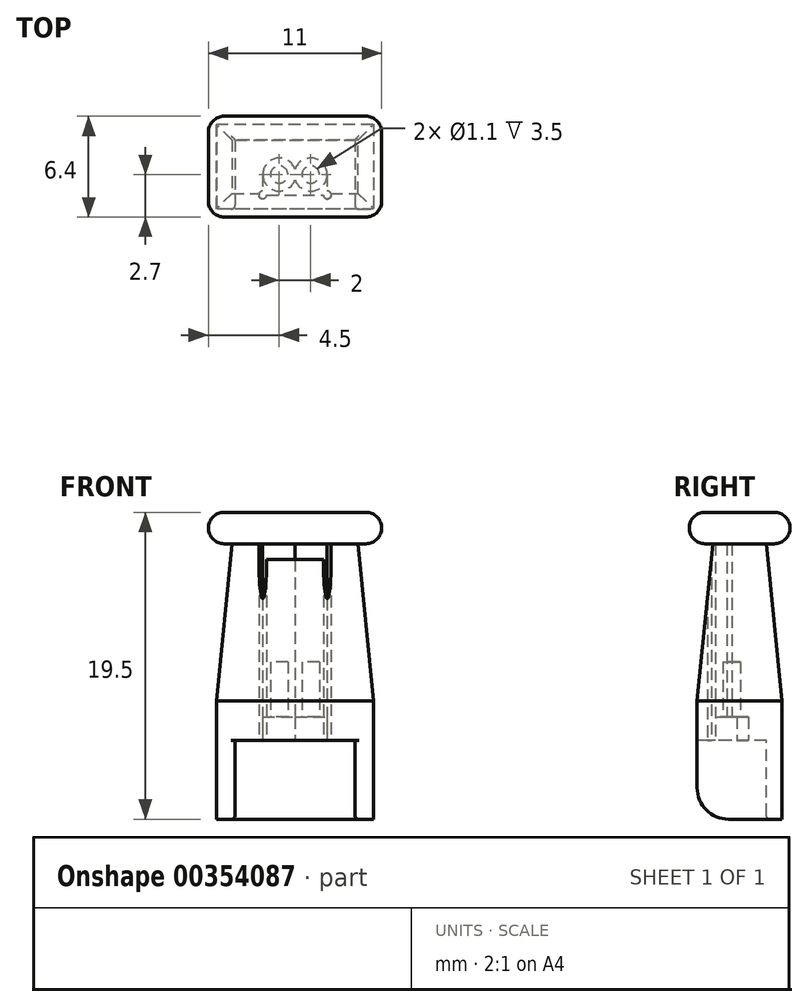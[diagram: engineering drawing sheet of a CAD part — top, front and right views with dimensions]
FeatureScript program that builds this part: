
annotation { "Feature Type Name" : "Feature", "Feature Type Description" : "" }
export const myFeature = defineFeature(function(context is Context, id is Id, definition is map)
    precondition{}
    {
        {
            var Q0;
            Q0=qCreatedBy(makeId("Top.planeOp"),FACE);
            var sketch = newSketch(context, id + "F0", { "sketchPlane" : qUnion([Q0])});
            skCircle(sketch, "E0", {"center": v(1, 0) * mm, "radius": 1.05 * mm});
            skCircle(sketch, "E1.MirrorC", {"center": v(-1, 0) * mm, "radius": 1.05 * mm});
            skLineSegment(sketch, "E2.top", {"start": v(-3.8, -2.2) * mm, "end": v(3.8, -2.2) * mm});
            skCircle(sketch, "E3", {"center": v(-2.05, 1.3) * mm, "radius": 0.25 * mm, "construction": true});
            skCircle(sketch, "E4.MirrorC", {"center": v(2.05, 1.3) * mm, "radius": 0.25 * mm, "construction": true});
            skCircle(sketch, "E5.MirrorC", {"center": v(-2.05, -1.3) * mm, "radius": 0.25 * mm, "construction": true});
            skCircle(sketch, "E6.MirrorC", {"center": v(2.05, -1.3) * mm, "radius": 0.25 * mm, "construction": true});
            skLineSegment(sketch, "E7", {"start": v(-1, 0) * mm, "end": v(1, 0) * mm, "construction": true});
            skPoint(sketch, "E8", {"position": v(0, 0) * mm});
            skLineSegment(sketch, "E9.bottom", {"start": v(2.05, 1.3) * mm, "end": v(-2.05, 1.3) * mm, "construction": true});
            skLineSegment(sketch, "E9.top", {"start": v(2.05, -1.3) * mm, "end": v(-2.05, -1.3) * mm, "construction": true});
            skLineSegment(sketch, "E9.left", {"start": v(2.05, 1.3) * mm, "end": v(2.05, -1.3) * mm, "construction": true});
            skLineSegment(sketch, "E9.right", {"start": v(-2.05, 1.3) * mm, "end": v(-2.05, -1.3) * mm, "construction": true});
            skArc(sketch, "E10", {"start": v(-1.8, 1.3) * mm, "mid": v(-2.23, 1.48) * mm, "end": v(-2.05, 1.05) * mm});
            skArc(sketch, "E11.MirrorCS", {"start": v(1.8, 1.3) * mm, "mid": v(2.23, 1.48) * mm, "end": v(2.05, 1.05) * mm});
            skArc(sketch, "E12.MirrorCS", {"start": v(-1.8, -1.3) * mm, "mid": v(-2.23, -1.48) * mm, "end": v(-2.05, -1.05) * mm});
            skArc(sketch, "E13.MirrorCS", {"start": v(1.8, -1.3) * mm, "mid": v(2.23, -1.48) * mm, "end": v(2.05, -1.05) * mm});
            skLineSegment(sketch, "E14", {"start": v(-2.05, 1.05) * mm, "end": v(-2.05, -1.05) * mm});
            skLineSegment(sketch, "E15", {"start": v(2.05, 1.05) * mm, "end": v(2.05, -1.05) * mm});
            skLineSegment(sketch, "E16", {"start": v(-1.8, 1.3) * mm, "end": v(1.8, 1.3) * mm});
            skLineSegment(sketch, "E17", {"start": v(-1.8, -1.3) * mm, "end": v(1.8, -1.3) * mm});
            skCircle(sketch, "E18", {"center": v(-1, 0) * mm, "radius": 0.55 * mm});
            skCircle(sketch, "E19", {"center": v(1, 0) * mm, "radius": 0.55 * mm});
            skPoint(sketch, "E20", {"position": v(0, -2.2) * mm});
            skLineSegment(sketch, "E21", {"start": v(0, 0) * mm, "end": v(0, -2.2) * mm, "construction": true});
            skLineSegment(sketch, "E22.MirrorCS", {"start": v(-3.8, 2.2) * mm, "end": v(3.8, 2.2) * mm});
            skLineSegment(sketch, "E23", {"start": v(3.8, 2.2) * mm, "end": v(3.8, -2.2) * mm});
            skLineSegment(sketch, "E24.bottom", {"start": v(-3.8, 2.2) * mm, "end": v(-5, 2.2) * mm});
            skLineSegment(sketch, "E24.top", {"start": v(-3.8, -2.2) * mm, "end": v(-5, -2.2) * mm});
            skLineSegment(sketch, "E24.left", {"start": v(-3.8, 2.2) * mm, "end": v(-3.8, -2.2) * mm});
            skLineSegment(sketch, "E24.right", {"start": v(-5, 2.2) * mm, "end": v(-5, -2.2) * mm});
            skLineSegment(sketch, "E25.MirrorCS", {"start": v(3.8, 2.2) * mm, "end": v(5, 2.2) * mm});
            skLineSegment(sketch, "E26.MirrorCS", {"start": v(5, 2.2) * mm, "end": v(5, -2.2) * mm});
            skLineSegment(sketch, "E27.MirrorCS", {"start": v(3.8, -2.2) * mm, "end": v(5, -2.2) * mm});
            skLineSegment(sketch, "E28", {"start": v(-5, 2.2) * mm, "end": v(-5, 3.2) * mm});
            skLineSegment(sketch, "E29.MirrorCS", {"start": v(5, 2.2) * mm, "end": v(5, 3.2) * mm});
            skLineSegment(sketch, "E30", {"start": v(-5, 3.2) * mm, "end": v(5, 3.2) * mm});
            skSolve(sketch);
        }
        {
            var Q0;
            Q0=makeQuery(id+"F0.imprint","IMPRINT",FACE,{"disambiguationData":[TD([[makeQuery(id+"F0.imprint","IMPRINT",EDGE,{"derivedFrom":sQuery(id+"F0.wireOp",EDGE,"E22.MirrorCS")}),1.0]])]});
            var Q1;
            Q1=makeQuery(id+"F0.imprint","IMPRINT",FACE,{"disambiguationData":[TD([[makeQuery(id+"F0.imprint","IMPRINT",EDGE,{"derivedFrom":sQuery(id+"F0.wireOp",EDGE,"E24.bottom")}),1.0]])]});
            var Q2;
            Q2=makeQuery(id+"F0.imprint","IMPRINT",FACE,{"disambiguationData":[TD([[makeQuery(id+"F0.imprint","IMPRINT",EDGE,{"derivedFrom":sQuery(id+"F0.wireOp",EDGE,"E2.top")}),1.0]])]});
            var Q3;
            Q3=makeQuery(id+"F0.imprint","IMPRINT",FACE,{"disambiguationData":[TD([[makeQuery(id+"F0.imprint","IMPRINT",EDGE,{"derivedFrom":sQuery(id+"F0.wireOp",EDGE,"E23")}),1.0]])]});
            var Q4;
            {var subQ0=sQuery(id+"F0.wireOp",EDGE,"E10");Q4=makeQuery(id+"F0.imprint","IMPRINT",FACE,{"disambiguationData":[TD([[makeQuery(id+"F0.imprint","IMPRINT",EDGE,{"derivedFrom":subQ0}),1.0]])]});}
            var Q5;
            {var subQ0=sQuery(id+"F0.wireOp",EDGE,"E12.MirrorCS");Q5=makeQuery(id+"F0.imprint","IMPRINT",FACE,{"disambiguationData":[TD([[makeQuery(id+"F0.imprint","IMPRINT",EDGE,{"derivedFrom":subQ0}),-1.0]])]});}
            var Q6;
            Q6=makeQuery(id+"F0.imprint","IMPRINT",FACE,{"disambiguationData":[TD([[makeQuery(id+"F0.imprint","IMPRINT",EDGE,{"derivedFrom":sQuery(id+"F0.wireOp",EDGE,"E18")}),-1.0]])]});
            var Q7;
            Q7=makeQuery(id+"F0.imprint","IMPRINT",FACE,{"disambiguationData":[TD([[makeQuery(id+"F0.imprint","IMPRINT",EDGE,{"derivedFrom":sQuery(id+"F0.wireOp",EDGE,"E19")}),-1.0]])]});
            var Q8;
            Q8=makeQuery(id+"F0.imprint","IMPRINT",FACE,{"disambiguationData":[TD([[makeQuery(id+"F0.imprint","IMPRINT",EDGE,{"derivedFrom":sQuery(id+"F0.wireOp",EDGE,"E18")}),1.0]])]});
            var Q9;
            Q9=makeQuery(id+"F0.imprint","IMPRINT",FACE,{"disambiguationData":[TD([[makeQuery(id+"F0.imprint","IMPRINT",EDGE,{"derivedFrom":sQuery(id+"F0.wireOp",EDGE,"E19")}),1.0]])]});
            var Q10;
            {var subQ0=sQuery(id+"F0.wireOp",EDGE,"E1.MirrorC");var subQ1=sQuery(id+"F0.wireOp",EDGE,"E0");var subQ2=makeQuery(id+"F0.imprint","INTERSECT",VERTEX,{"disambiguationData":[OD(0.0)],"derivedFrom":[subQ1,subQ0]});Q10=makeQuery(id+"F0.imprint","IMPRINT",FACE,{"disambiguationData":[TD([[makeQuery(id+"F0.imprint","IMPRINT",EDGE,{"disambiguationData":[TD([[subQ2,-1.0]])],"derivedFrom":subQ1}),1.0]])]});}
            extrude(context, id + "F1", {"entities" : qUnion([Q0, Q1, Q2, Q3, Q4, Q5, Q6, Q7, Q8, Q9, Q10]), "depth" : 12.5 * mm, "offsetDistance" : 25 * mm});
        }
        {
            var Q0;
            Q0=makeQuery(id+"F0.imprint","IMPRINT",FACE,{"disambiguationData":[TD([[makeQuery(id+"F0.imprint","IMPRINT",EDGE,{"derivedFrom":sQuery(id+"F0.wireOp",EDGE,"E24.bottom")}),1.0]])]});
            var Q1;
            Q1=makeQuery(id+"F0.imprint","IMPRINT",FACE,{"disambiguationData":[TD([[makeQuery(id+"F0.imprint","IMPRINT",EDGE,{"derivedFrom":sQuery(id+"F0.wireOp",EDGE,"E23")}),1.0]])]});
            var Q2;
            Q2=makeQuery(id+"F0.imprint","IMPRINT",FACE,{"disambiguationData":[TD([[makeQuery(id+"F0.imprint","IMPRINT",EDGE,{"derivedFrom":sQuery(id+"F0.wireOp",EDGE,"E22.MirrorCS")}),1.0]])]});
            extrude(context, id + "F2", {"entities" : qUnion([Q0, Q1, Q2]), "operationType" : NewBodyOperationType.ADD, "oppositeDirection" : true, "depth" : 5 * mm, "offsetDistance" : 25 * mm});
        }
        {
            var Q0;
            Q0=makeQuery(id+"F0.imprint","IMPRINT",FACE,{"disambiguationData":[TD([[makeQuery(id+"F0.imprint","IMPRINT",EDGE,{"derivedFrom":sQuery(id+"F0.wireOp",EDGE,"E18")}),-1.0]])]});
            var Q1;
            Q1=makeQuery(id+"F0.imprint","IMPRINT",FACE,{"disambiguationData":[TD([[makeQuery(id+"F0.imprint","IMPRINT",EDGE,{"derivedFrom":sQuery(id+"F0.wireOp",EDGE,"E19")}),-1.0]])]});
            var Q2;
            {var subQ0=sQuery(id+"F0.wireOp",EDGE,"E1.MirrorC");var subQ1=sQuery(id+"F0.wireOp",EDGE,"E0");var subQ2=makeQuery(id+"F0.imprint","INTERSECT",VERTEX,{"disambiguationData":[OD(0.0)],"derivedFrom":[subQ1,subQ0]});Q2=makeQuery(id+"F0.imprint","IMPRINT",FACE,{"disambiguationData":[TD([[makeQuery(id+"F0.imprint","IMPRINT",EDGE,{"disambiguationData":[TD([[subQ2,-1.0]])],"derivedFrom":subQ1}),1.0]])]});}
            extrude(context, id + "F3", {"entities" : qUnion([Q0, Q1, Q2]), "operationType" : NewBodyOperationType.REMOVE, "depth" : 1.5 * mm, "offsetDistance" : 25 * mm});
        }
        {
            var Q0;
            Q0=makeQuery(id+"F0.imprint","IMPRINT",FACE,{"disambiguationData":[TD([[makeQuery(id+"F0.imprint","IMPRINT",EDGE,{"derivedFrom":sQuery(id+"F0.wireOp",EDGE,"E18")}),1.0]])]});
            var Q1;
            Q1=makeQuery(id+"F0.imprint","IMPRINT",FACE,{"disambiguationData":[TD([[makeQuery(id+"F0.imprint","IMPRINT",EDGE,{"derivedFrom":sQuery(id+"F0.wireOp",EDGE,"E19")}),1.0]])]});
            extrude(context, id + "F4", {"entities" : qUnion([Q0, Q1]), "operationType" : NewBodyOperationType.REMOVE, "depth" : 5 * mm, "offsetDistance" : 25 * mm});
        }
        {
            var Q0;
            Q0=makeQuery(id+"F2.opExtrude","CAP_EDGE",EDGE,{"disambiguationData":[OSD([sQuery(id+"F0.wireOp",EDGE,"E27.MirrorCS")])],"isStart":false});
            var Q1;
            Q1=makeQuery(id+"F2.opExtrude","CAP_EDGE",EDGE,{"disambiguationData":[OSD([sQuery(id+"F0.wireOp",EDGE,"E24.top")])],"isStart":false});
            fillet(context, id + "F5", {"entities" : qUnion([Q0, Q1]), "radius" : 2 * mm, "tangentPropagation" : true, "allowEdgeOverflow" : false});
        }
        {
            var Q0;
            Q0=makeQuery(id+"F3.boolean.opBoolean","COPY",EDGE,{"derivedFrom":makeQuery(id+"F3.opExtrude","CAP_EDGE",EDGE,{"disambiguationData":[OSD([sQuery(id+"F0.wireOp",EDGE,"E19")])],"isStart":false})});
            var Q1;
            Q1=makeQuery(id+"F3.boolean.opBoolean","COPY",EDGE,{"derivedFrom":makeQuery(id+"F3.opExtrude","CAP_EDGE",EDGE,{"disambiguationData":[OSD([sQuery(id+"F0.wireOp",EDGE,"E0")])],"isStart":true})});
            var Q2;
            Q2=makeQuery(id+"F3.boolean.opBoolean","COPY",EDGE,{"derivedFrom":makeQuery(id+"F3.opExtrude","CAP_EDGE",EDGE,{"disambiguationData":[OSD([sQuery(id+"F0.wireOp",EDGE,"E18")])],"isStart":false})});
            var Q3;
            Q3=makeQuery(id+"F3.boolean.opBoolean","COPY",EDGE,{"derivedFrom":makeQuery(id+"F3.opExtrude","CAP_EDGE",EDGE,{"disambiguationData":[OSD([sQuery(id+"F0.wireOp",EDGE,"E1.MirrorC")])],"isStart":true})});
            var Q4;
            Q4=makeQuery(id+"F2.opExtrude","CAP_EDGE",EDGE,{"disambiguationData":[OSD([sQuery(id+"F0.wireOp",EDGE,"E24.left")])],"isStart":false});
            var Q5;
            Q5=makeQuery(id+"F2.opExtrude","CAP_EDGE",EDGE,{"disambiguationData":[OSD([sQuery(id+"F0.wireOp",EDGE,"E22.MirrorCS")])],"isStart":false});
            var Q6;
            Q6=makeQuery(id+"F2.opExtrude","CAP_EDGE",EDGE,{"disambiguationData":[OSD([sQuery(id+"F0.wireOp",EDGE,"E23")])],"isStart":false});
            var Q7;
            Q7=makeQuery(id+"F2.opExtrude","SWEPT_EDGE",EDGE,{"disambiguationData":[OSD([sQuery(id+"F0.wireOp",EDGE,"E2.top"),sQuery(id+"F0.wireOp",EDGE,"E24.top"),sQuery(id+"F0.wireOp",EDGE,"E24.left")])]});
            var Q8;
            Q8=makeQuery(id+"F2.opExtrude","SWEPT_EDGE",EDGE,{"disambiguationData":[OSD([sQuery(id+"F0.wireOp",EDGE,"E2.top"),sQuery(id+"F0.wireOp",EDGE,"E23"),sQuery(id+"F0.wireOp",EDGE,"E27.MirrorCS")])]});
            fillet(context, id + "F6", {"entities" : qUnion([Q0, Q1, Q2, Q3, Q4, Q5, Q6, Q7, Q8]), "radius" : .25 * mm, "tangentPropagation" : true, "allowEdgeOverflow" : false});
        }
        {
            var Q0;
            Q0=makeQuery(id+"F1.opExtrude","CAP_EDGE",EDGE,{"disambiguationData":[OSD([sQuery(id+"F0.wireOp",EDGE,"E2.top"),sQuery(id+"F0.wireOp",EDGE,"E24.top"),sQuery(id+"F0.wireOp",EDGE,"E27.MirrorCS")])],"isStart":false});
            var Q1;
            Q1=makeQuery(id+"F1.opExtrude","CAP_EDGE",EDGE,{"disambiguationData":[OSD([sQuery(id+"F0.wireOp",EDGE,"E24.right"),sQuery(id+"F0.wireOp",EDGE,"E28")])],"isStart":false});
            var Q2;
            Q2=makeQuery(id+"F1.opExtrude","CAP_EDGE",EDGE,{"disambiguationData":[OSD([sQuery(id+"F0.wireOp",EDGE,"E26.MirrorCS"),sQuery(id+"F0.wireOp",EDGE,"E29.MirrorCS")])],"isStart":false});
            var Q3;
            Q3=makeQuery(id+"F1.opExtrude","CAP_EDGE",EDGE,{"disambiguationData":[OSD([sQuery(id+"F0.wireOp",EDGE,"E30")])],"isStart":false});
            chamfer(context, id + "F7", {"entities" : qUnion([Q0, Q1, Q2, Q3]), "chamferType" : ChamferType.TWO_OFFSETS, "width1" : 10 * mm, "oppositeDirection" : false, "width2" : 1 * mm, "tangentPropagation" : true});
        }
        {
            var Q0;
            Q0=makeQuery(id+"F1.opExtrude","CAP_FACE",FACE,{"disambiguationData":[OSD([sQuery(id+"F0.wireOp",EDGE,"E2.top"),sQuery(id+"F0.wireOp",EDGE,"E24.top"),sQuery(id+"F0.wireOp",EDGE,"E24.right"),sQuery(id+"F0.wireOp",EDGE,"E26.MirrorCS"),sQuery(id+"F0.wireOp",EDGE,"E27.MirrorCS"),sQuery(id+"F0.wireOp",EDGE,"E28"),sQuery(id+"F0.wireOp",EDGE,"E29.MirrorCS"),sQuery(id+"F0.wireOp",EDGE,"E30")])],"isStart":false});
            var sketch = newSketch(context, id + "F8", { "sketchPlane" : qUnion([Q0])});
            skLineSegment(sketch, "E31.bottom", {"start": v(4, -1.2) * mm, "end": v(-4, -1.2) * mm, "construction": true});
            skLineSegment(sketch, "E31.top", {"start": v(4, 2.2) * mm, "end": v(-4, 2.2) * mm, "construction": true});
            skLineSegment(sketch, "E31.left", {"start": v(4, -1.2) * mm, "end": v(4, 2.2) * mm, "construction": true});
            skLineSegment(sketch, "E31.right", {"start": v(-4, -1.2) * mm, "end": v(-4, 2.2) * mm, "construction": true});
            skLineSegment(sketch, "E32.0", {"start": v(5.5, -2.7) * mm, "end": v(-5.5, -2.7) * mm});
            skLineSegment(sketch, "E32.1", {"start": v(5.5, -2.7) * mm, "end": v(5.5, 3.7) * mm});
            skLineSegment(sketch, "E32.2", {"start": v(5.5, 3.7) * mm, "end": v(-5.5, 3.7) * mm});
            skLineSegment(sketch, "E32.3", {"start": v(-5.5, -2.7) * mm, "end": v(-5.5, 3.7) * mm});
            skSolve(sketch);
        }
        {
            var Q0;
            Q0=makeQuery(id+"F8.imprint","IMPRINT",FACE,{"disambiguationData":[TD([[makeQuery(id+"F8.imprint","IMPRINT",EDGE,{"derivedFrom":sQuery(id+"F8.wireOp",EDGE,"E32.0")}),-1.0]])]});
            var Q1;
            {var subQ0=sQuery(id+"F0.wireOp",EDGE,"E30");var subQ1=sQuery(id+"F0.wireOp",EDGE,"E29.MirrorCS");var subQ2=sQuery(id+"F0.wireOp",EDGE,"E28");var subQ3=sQuery(id+"F0.wireOp",EDGE,"E27.MirrorCS");var subQ4=sQuery(id+"F0.wireOp",EDGE,"E26.MirrorCS");var subQ5=sQuery(id+"F0.wireOp",EDGE,"E24.right");var subQ6=sQuery(id+"F0.wireOp",EDGE,"E24.top");var subQ7=sQuery(id+"F0.wireOp",EDGE,"E2.top");var subQ8=makeQuery(id+"F1.opExtrude","CAP_FACE",FACE,{"disambiguationData":[OSD([subQ7,subQ6,subQ5,subQ4,subQ3,subQ2,subQ1,subQ0])],"isStart":false});Q1=makeQuery(id+"F8.imprint","IMPRINT",FACE,{"disambiguationData":[TD([[makeQuery(id+"F8.imprint","IMPRINT",EDGE,{"derivedFrom":makeQuery(id+"F7.opChamfer","BLEND_EDGE",EDGE,{"blendedFrom":[makeQuery(id+"F1.opExtrude","CAP_EDGE",EDGE,{"disambiguationData":[OSD([subQ0])],"isStart":false}),subQ8],"blendedInto":[subQ8]})}),1.0]])]});}
            extrude(context, id + "F9", {"entities" : qUnion([Q0, Q1]), "operationType" : NewBodyOperationType.ADD, "depth" : 2 * mm, "offsetDistance" : 25 * mm});
        }
        {
            var Q0;
            Q0=makeQuery(id+"F9.opExtrude","SWEPT_EDGE",EDGE,{"disambiguationData":[OSD([sQuery(id+"F8.wireOp",EDGE,"E32.0"),sQuery(id+"F8.wireOp",EDGE,"E32.1")])]});
            var Q1;
            Q1=makeQuery(id+"F9.opExtrude","SWEPT_EDGE",EDGE,{"disambiguationData":[OSD([sQuery(id+"F8.wireOp",EDGE,"E32.0"),sQuery(id+"F8.wireOp",EDGE,"E32.3")])]});
            var Q2;
            Q2=makeQuery(id+"F9.opExtrude","SWEPT_EDGE",EDGE,{"disambiguationData":[OSD([sQuery(id+"F8.wireOp",EDGE,"E32.1"),sQuery(id+"F8.wireOp",EDGE,"E32.2")])]});
            var Q3;
            Q3=makeQuery(id+"F9.opExtrude","SWEPT_EDGE",EDGE,{"disambiguationData":[OSD([sQuery(id+"F8.wireOp",EDGE,"E32.2"),sQuery(id+"F8.wireOp",EDGE,"E32.3")])]});
            var Q4;
            Q4=makeQuery(id+"F9.opExtrude","CAP_EDGE",EDGE,{"disambiguationData":[OSD([sQuery(id+"F8.wireOp",EDGE,"E32.2")])],"isStart":true});
            var Q5;
            Q5=makeQuery(id+"F9.opExtrude","CAP_EDGE",EDGE,{"disambiguationData":[OSD([sQuery(id+"F8.wireOp",EDGE,"E32.2")])],"isStart":false});
            var Q6;
            Q6=makeQuery(id+"F9.opExtrude","CAP_EDGE",EDGE,{"disambiguationData":[OSD([sQuery(id+"F8.wireOp",EDGE,"E32.3")])],"isStart":false});
            var Q7;
            Q7=makeQuery(id+"F9.opExtrude","CAP_EDGE",EDGE,{"disambiguationData":[OSD([sQuery(id+"F8.wireOp",EDGE,"E32.1")])],"isStart":false});
            var Q8;
            Q8=makeQuery(id+"F9.opExtrude","CAP_EDGE",EDGE,{"disambiguationData":[OSD([sQuery(id+"F8.wireOp",EDGE,"E32.0")])],"isStart":false});
            var Q9;
            Q9=makeQuery(id+"F9.opExtrude","CAP_EDGE",EDGE,{"disambiguationData":[OSD([sQuery(id+"F8.wireOp",EDGE,"E32.1")])],"isStart":true});
            var Q10;
            Q10=makeQuery(id+"F9.opExtrude","CAP_EDGE",EDGE,{"disambiguationData":[OSD([sQuery(id+"F8.wireOp",EDGE,"E32.0")])],"isStart":true});
            var Q11;
            Q11=makeQuery(id+"F9.opExtrude","CAP_EDGE",EDGE,{"disambiguationData":[OSD([sQuery(id+"F8.wireOp",EDGE,"E32.3")])],"isStart":true});
            fillet(context, id + "F10", {"entities" : qUnion([Q0, Q1, Q2, Q3, Q4, Q5, Q6, Q7, Q8, Q9, Q10, Q11]), "radius" : 1 * mm, "tangentPropagation" : true, "allowEdgeOverflow" : false});
        }
    });
